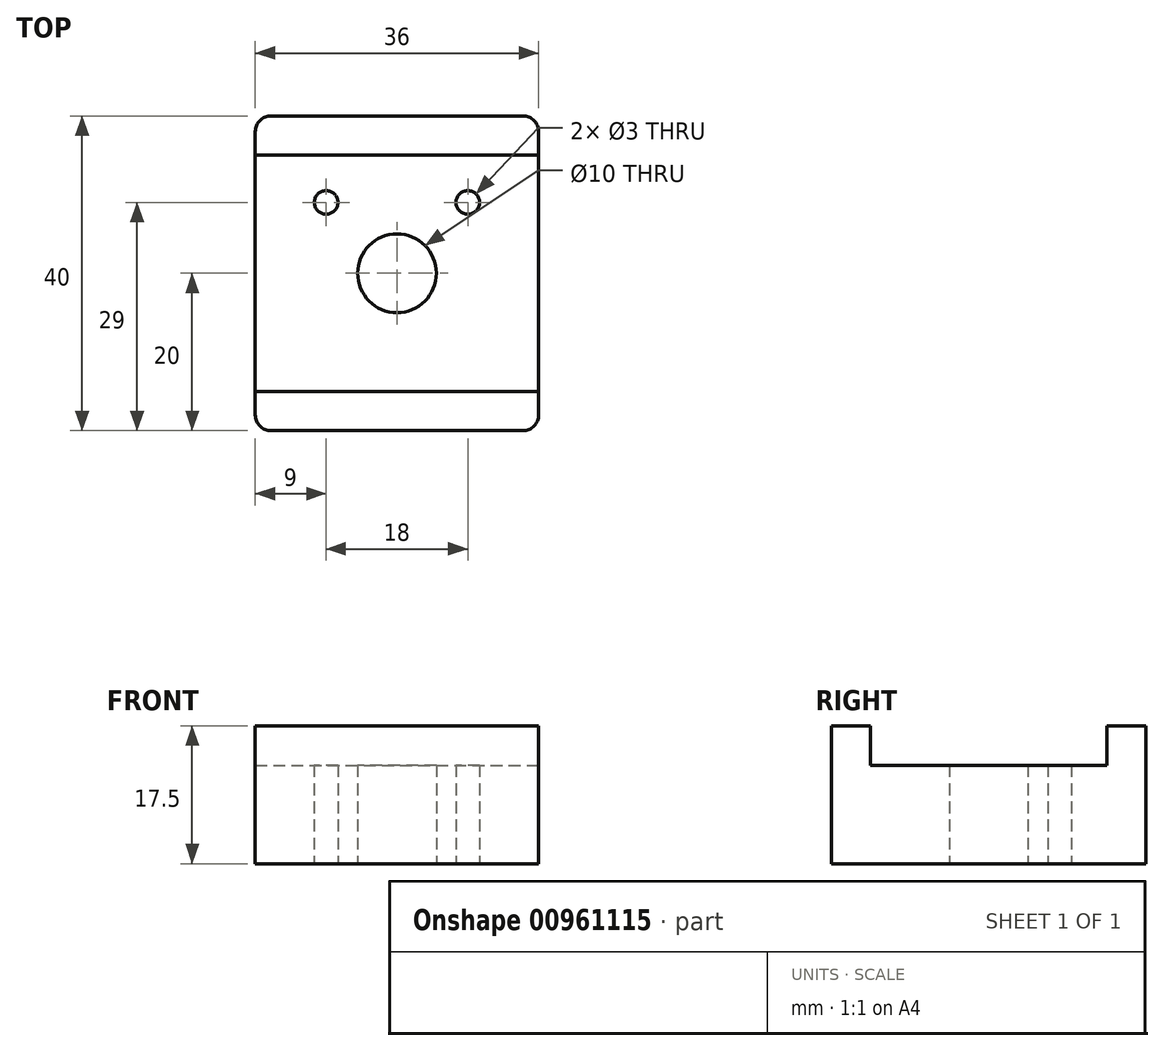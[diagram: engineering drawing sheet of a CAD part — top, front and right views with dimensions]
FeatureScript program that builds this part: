
annotation { "Feature Type Name" : "Feature", "Feature Type Description" : "" }
export const myFeature = defineFeature(function(context is Context, id is Id, definition is map)
    precondition{}
    {
        {
            var Q0;
            Q0=qCreatedBy(makeId("Top.planeOp"),FACE);
            var sketch = newSketch(context, id + "F0", { "sketchPlane" : qUnion([Q0])});
            skLineSegment(sketch, "E0.bottom", {"start": v(16, 20) * mm, "end": v(-16, 20) * mm});
            skLineSegment(sketch, "E0.top", {"start": v(16, -20) * mm, "end": v(-16, -20) * mm});
            skLineSegment(sketch, "E0.left", {"start": v(18, 18) * mm, "end": v(18, -18) * mm});
            skLineSegment(sketch, "E0.right", {"start": v(-18, 18) * mm, "end": v(-18, -18) * mm});
            skPoint(sketch, "E0.middle", {"position": v(0, 0) * mm});
            skPoint(sketch, "E1.visualSharp", {"position": v(-18, 20) * mm});
            skArc(sketch, "E1.filletArc", {"start": v(-16, 20) * mm, "mid": v(-17.41, 19.41) * mm, "end": v(-18, 18) * mm});
            skPoint(sketch, "E2.visualSharp", {"position": v(18, 20) * mm});
            skArc(sketch, "E2.filletArc", {"start": v(18, 18) * mm, "mid": v(17.41, 19.41) * mm, "end": v(16, 20) * mm});
            skPoint(sketch, "E3.visualSharp", {"position": v(18, -20) * mm});
            skArc(sketch, "E3.filletArc", {"start": v(16, -20) * mm, "mid": v(17.41, -19.41) * mm, "end": v(18, -18) * mm});
            skPoint(sketch, "E4.visualSharp", {"position": v(-18, -20) * mm});
            skArc(sketch, "E4.filletArc", {"start": v(-18, -18) * mm, "mid": v(-17.41, -19.41) * mm, "end": v(-16, -20) * mm});
            skCircle(sketch, "E5", {"center": v(-9, 9) * mm, "radius": 1.5 * mm});
            skCircle(sketch, "E6.MirrorC", {"center": v(9, 9) * mm, "radius": 1.5 * mm});
            skLineSegment(sketch, "E7.bottom", {"start": v(-13, 13) * mm, "end": v(13, 13) * mm, "construction": true});
            skLineSegment(sketch, "E7.top", {"start": v(-13, -13) * mm, "end": v(13, -13) * mm, "construction": true});
            skLineSegment(sketch, "E7.left", {"start": v(-13, 13) * mm, "end": v(-13, -13) * mm, "construction": true});
            skLineSegment(sketch, "E7.right", {"start": v(13, 13) * mm, "end": v(13, -13) * mm, "construction": true});
            skCircle(sketch, "E8", {"center": v(0, 0) * mm, "radius": 5 * mm});
            skSolve(sketch);
        }
        {
            var Q0;
            Q0=makeQuery(id+"F0.imprint","IMPRINT",FACE,{"disambiguationData":[TD([[makeQuery(id+"F0.imprint","IMPRINT",EDGE,{"derivedFrom":sQuery(id+"F0.wireOp",EDGE,"E0.bottom")}),1.0]])]});
            extrude(context, id + "F1", {"entities" : qUnion([Q0]), "depth" : 12.5 * mm, "offsetDistance" : 25 * mm});
        }
        {
            var Q0;
            Q0=makeQuery(id+"F1.opExtrude","CAP_FACE",FACE,{"disambiguationData":[OSD([sQuery(id+"F0.wireOp",EDGE,"E0.bottom"),sQuery(id+"F0.wireOp",EDGE,"E0.top"),sQuery(id+"F0.wireOp",EDGE,"E0.left"),sQuery(id+"F0.wireOp",EDGE,"E0.right"),sQuery(id+"F0.wireOp",EDGE,"E1.filletArc"),sQuery(id+"F0.wireOp",EDGE,"E2.filletArc"),sQuery(id+"F0.wireOp",EDGE,"E3.filletArc"),sQuery(id+"F0.wireOp",EDGE,"E4.filletArc"),sQuery(id+"F0.wireOp",EDGE,"E5"),sQuery(id+"F0.wireOp",EDGE,"E6.MirrorC"),sQuery(id+"F0.wireOp",EDGE,"E8")])],"isStart":false});
            var sketch = newSketch(context, id + "F2", { "sketchPlane" : qUnion([Q0])});
            skLineSegment(sketch, "E9", {"start": v(-18, 15) * mm, "end": v(18, 15) * mm});
            skLineSegment(sketch, "E10", {"start": v(-18, -15) * mm, "end": v(18, -15) * mm});
            skSolve(sketch);
        }
        {
            var Q0;
            {var subQ2=sQuery(id+"F2.wireOp",EDGE,"E9");Q0=makeQuery(id+"F2.imprint","IMPRINT",FACE,{"disambiguationData":[TD([[makeQuery(id+"F2.imprint","IMPRINT",EDGE,{"derivedFrom":subQ2}),1.0]])]});}
            var Q1;
            {var subQ2=sQuery(id+"F2.wireOp",EDGE,"E10");Q1=makeQuery(id+"F2.imprint","IMPRINT",FACE,{"disambiguationData":[TD([[makeQuery(id+"F2.imprint","IMPRINT",EDGE,{"derivedFrom":subQ2}),-1.0]])]});}
            extrude(context, id + "F3", {"entities" : qUnion([Q0, Q1]), "operationType" : NewBodyOperationType.ADD, "depth" : 5 * mm, "offsetDistance" : 25 * mm});
        }
    });
